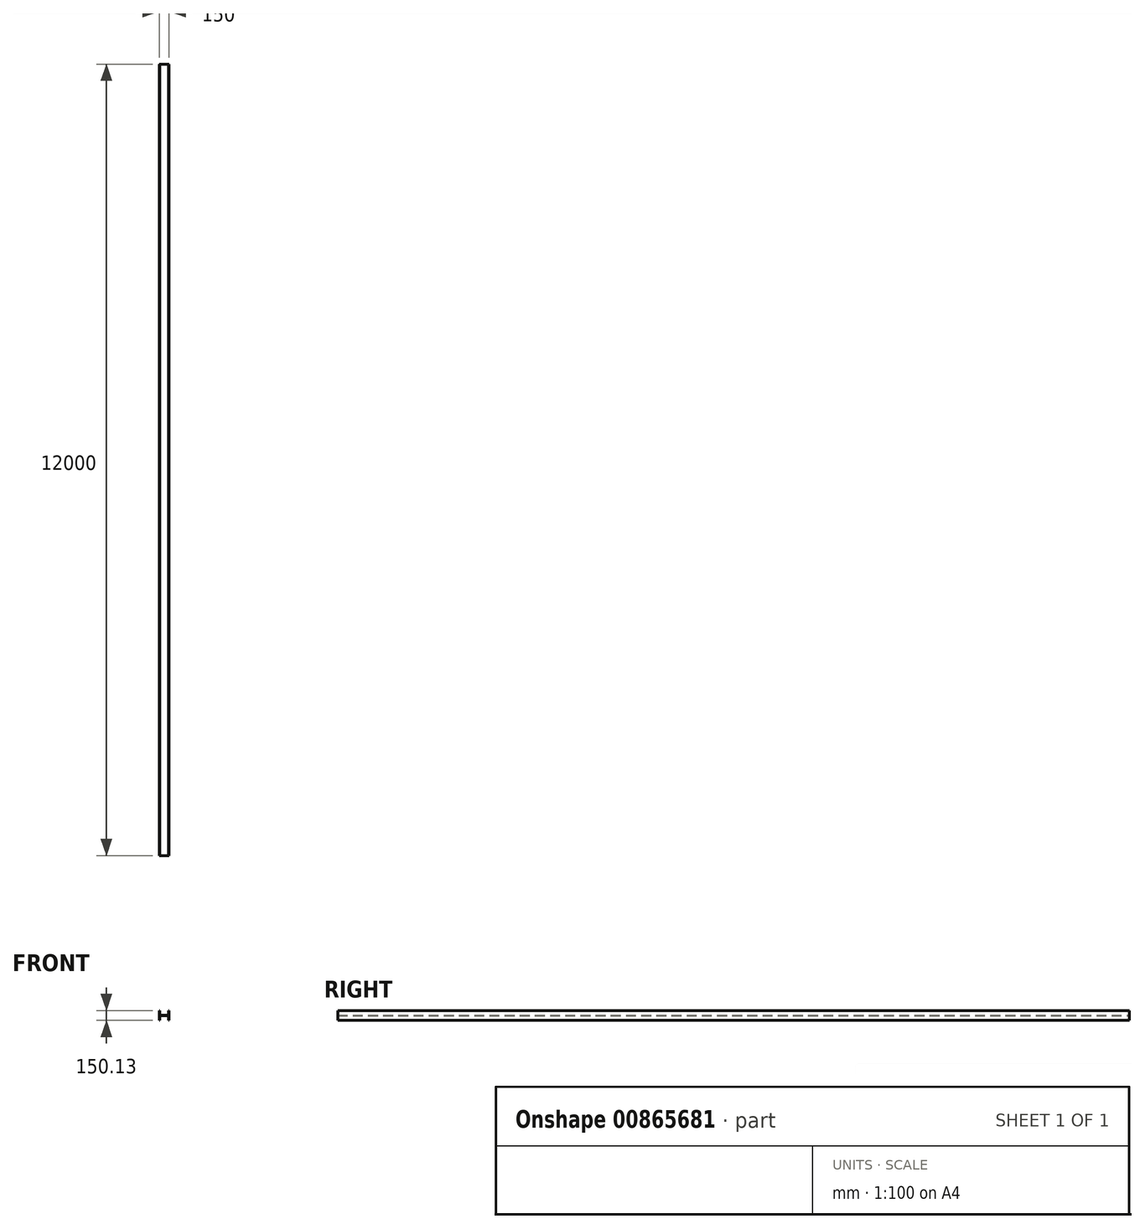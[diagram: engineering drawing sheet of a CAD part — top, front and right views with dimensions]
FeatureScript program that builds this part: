
annotation { "Feature Type Name" : "Feature", "Feature Type Description" : "" }
export const myFeature = defineFeature(function(context is Context, id is Id, definition is map)
    precondition{}
    {
        {
            var Q0;
            Q0=qCreatedBy(makeId("Front.planeOp"),FACE);
            var sketch = newSketch(context, id + "F0", { "sketchPlane" : qUnion([Q0])});
            skLineSegment(sketch, "E0.top", {"start": v(-75, -74.95) * mm, "end": v(-65, -74.95) * mm});
            skLineSegment(sketch, "E0.left", {"start": v(-75, 75.05) * mm, "end": v(-75, -74.95) * mm});
            skLineSegment(sketch, "E1", {"start": v(-65, -74.95) * mm, "end": v(-65, -14.5) * mm});
            skLineSegment(sketch, "E2", {"start": v(-65, 75.18) * mm, "end": v(-75, 75.05) * mm});
            skLineSegment(sketch, "E3.MirrorCS", {"start": v(65, -74.95) * mm, "end": v(65, -14.5) * mm});
            skLineSegment(sketch, "E4.MirrorCS", {"start": v(65, 75.18) * mm, "end": v(75, 75.05) * mm});
            skLineSegment(sketch, "E5.MirrorCS", {"start": v(75, 75.05) * mm, "end": v(75, -74.95) * mm});
            skLineSegment(sketch, "E6.MirrorCS", {"start": v(75, -74.95) * mm, "end": v(65, -74.95) * mm});
            skLineSegment(sketch, "E7", {"start": v(-54, 3.5) * mm, "end": v(54, 3.5) * mm});
            skLineSegment(sketch, "E8.MirrorCS", {"start": v(-54, -3.5) * mm, "end": v(54, -3.5) * mm});
            skLineSegment(sketch, "E9.trimOffspring", {"start": v(-65, 14.5) * mm, "end": v(-65, 75.18) * mm});
            skLineSegment(sketch, "E10.trimOffspring", {"start": v(65, 14.5) * mm, "end": v(65, 75.18) * mm});
            skPoint(sketch, "E11.visualSharp", {"position": v(-65, 3.5) * mm});
            skArc(sketch, "E11.filletArc", {"start": v(-65, 14.5) * mm, "mid": v(-61.78, 6.72) * mm, "end": v(-54, 3.5) * mm});
            skPoint(sketch, "E12.visualSharp", {"position": v(65, 3.5) * mm});
            skArc(sketch, "E12.filletArc", {"start": v(54, 3.5) * mm, "mid": v(61.78, 6.72) * mm, "end": v(65, 14.5) * mm});
            skPoint(sketch, "E13.visualSharp", {"position": v(65, -3.5) * mm});
            skArc(sketch, "E13.filletArc", {"start": v(65, -14.5) * mm, "mid": v(61.78, -6.72) * mm, "end": v(54, -3.5) * mm});
            skPoint(sketch, "E14.visualSharp", {"position": v(-65, -3.5) * mm});
            skArc(sketch, "E14.filletArc", {"start": v(-54, -3.5) * mm, "mid": v(-61.78, -6.72) * mm, "end": v(-65, -14.5) * mm});
            skSolve(sketch);
        }
        {
            var Q0;
            Q0=makeQuery(id+"F0.imprint","IMPRINT",FACE,{"disambiguationData":[TD([[makeQuery(id+"F0.imprint","IMPRINT",EDGE,{"derivedFrom":sQuery(id+"F0.wireOp",EDGE,"E0.top")}),1.0]])]});
            extrude(context, id + "F1", {"entities" : qUnion([Q0]), "depth" : 12000 * mm, "offsetDistance" : 25 * mm});
        }
    });
